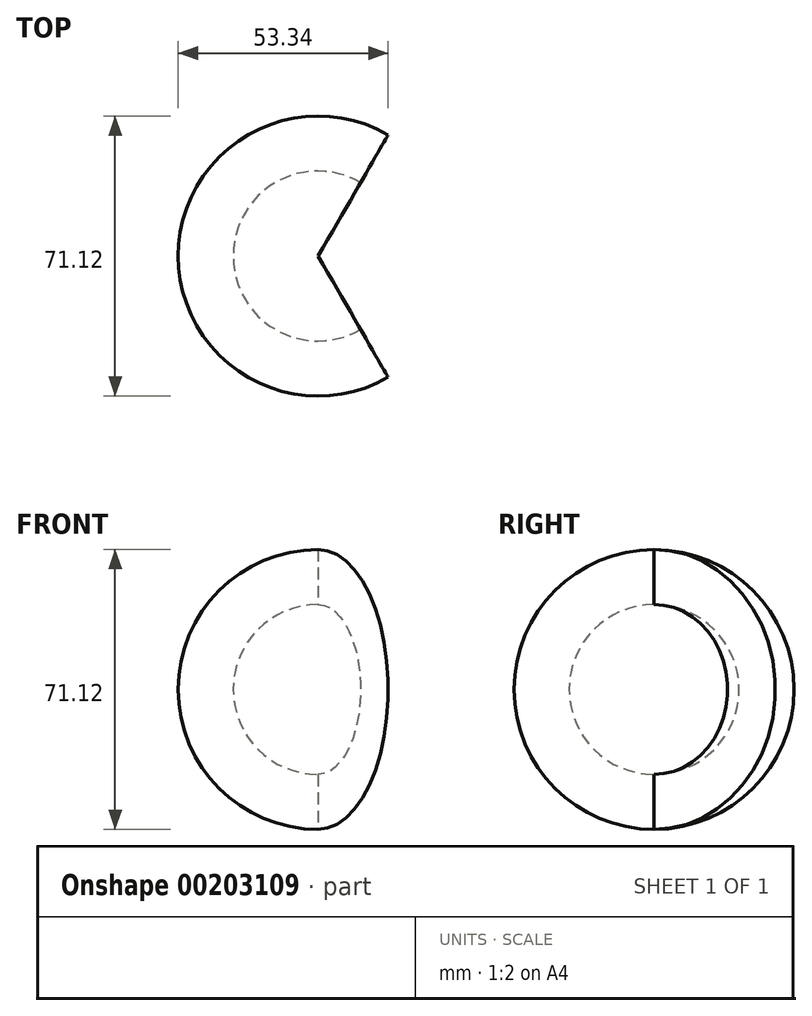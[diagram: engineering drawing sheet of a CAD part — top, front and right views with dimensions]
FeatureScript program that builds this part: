
annotation { "Feature Type Name" : "Feature", "Feature Type Description" : "" }
export const myFeature = defineFeature(function(context is Context, id is Id, definition is map)
    precondition{}
    {
        {
            var Q0;
            Q0=qCreatedBy(makeId("Front.planeOp"),FACE);
            var sketch = newSketch(context, id + "F0", { "sketchPlane" : qUnion([Q0])});
            skArc(sketch, "E0", {"start": v(0, 35.56) * mm, "mid": v(-35.56, 0) * mm, "end": v(0, -35.56) * mm});
            skLineSegment(sketch, "E1", {"start": v(0, 35.56) * mm, "end": v(0, -35.56) * mm});
            skSolve(sketch);
        }
        {
            var Q0;
            Q0=makeQuery(id+"F0.imprint","IMPRINT",FACE,{"disambiguationData":[TD([[makeQuery(id+"F0.imprint","IMPRINT",EDGE,{"derivedFrom":sQuery(id+"F0.wireOp",EDGE,"E0")}),1.0]])]});
            var Q1;
            Q1=sQuery(id+"F0.wireOp",EDGE,"E1");
            revolve(context, id + "F1", {"entities" : qUnion([Q0]), "axis" : qUnion([Q1]), "revolveType" : RevolveType.SYMMETRIC, "angle" : 240 * degree});
        }
        {
            var Q0;
            Q0=qCreatedBy(makeId("Front.planeOp"),FACE);
            var sketch = newSketch(context, id + "F2", { "sketchPlane" : qUnion([Q0])});
            skArc(sketch, "E2", {"start": v(0, 21.59) * mm, "mid": v(-21.59, 0) * mm, "end": v(0, -21.59) * mm});
            skLineSegment(sketch, "E3", {"start": v(0, 21.59) * mm, "end": v(0, -21.59) * mm});
            skSolve(sketch);
        }
        {
            var Q0;
            Q0 = qSketchRegion(id + "F2", true);
            var Q1;
            Q1=sQuery(id+"F2.wireOp",EDGE,"E3");
            revolve(context, id + "F3", {"operationType" : NewBodyOperationType.REMOVE, "entities" : qUnion([Q0]), "axis" : qUnion([Q1]), "revolveType" : RevolveType.FULL, "oppositeDirection" : true});
        }
    });
